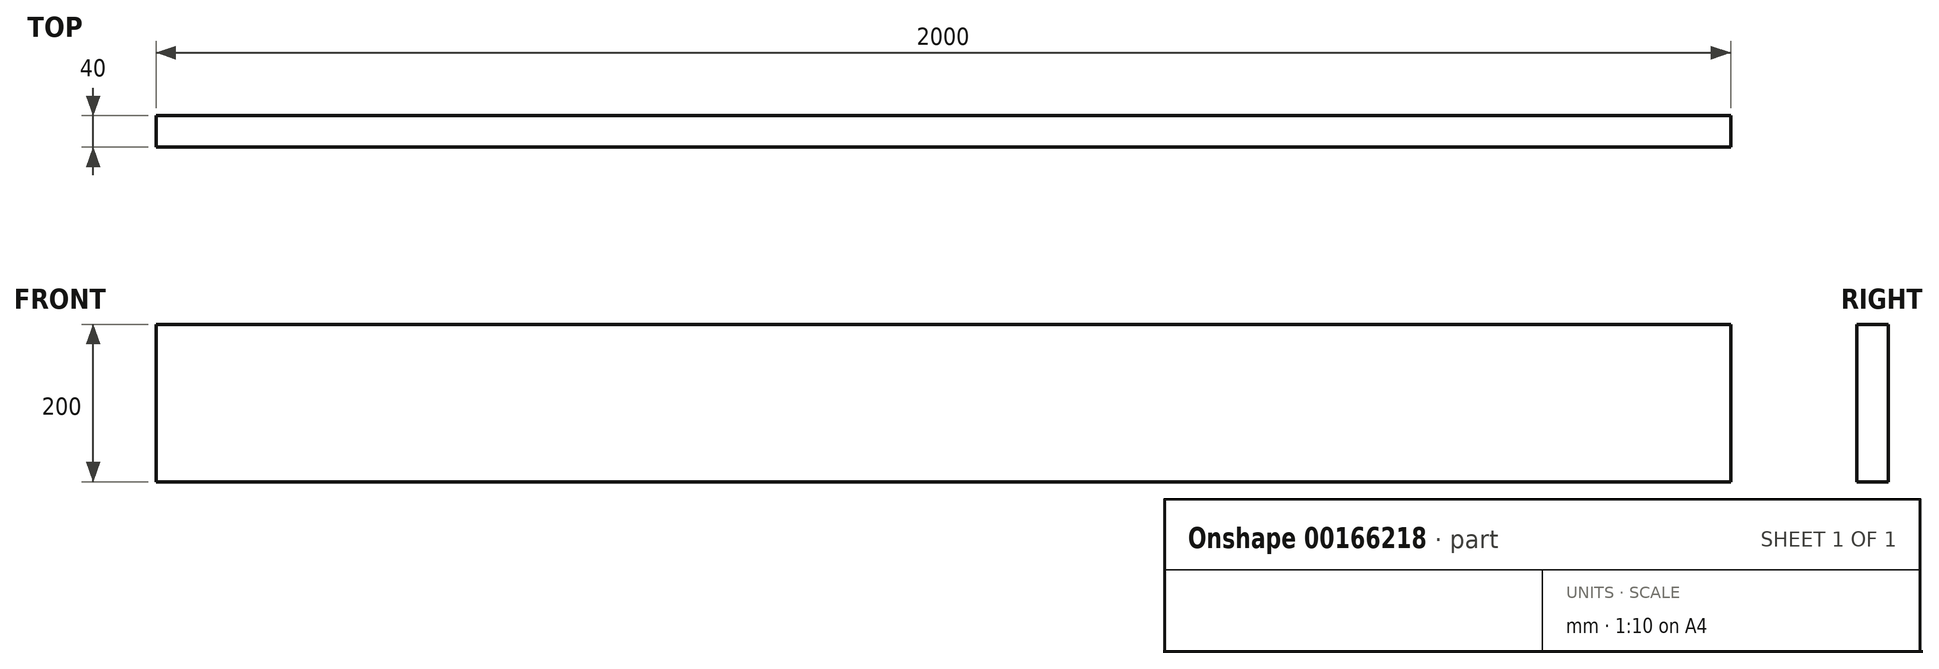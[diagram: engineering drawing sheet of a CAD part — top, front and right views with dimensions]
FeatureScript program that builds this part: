
annotation { "Feature Type Name" : "Feature", "Feature Type Description" : "" }
export const myFeature = defineFeature(function(context is Context, id is Id, definition is map)
    precondition{}
    {
        {
            var Q0;
            Q0=qCreatedBy(makeId("Front.planeOp"),FACE);
            var sketch = newSketch(context, id + "F0", { "sketchPlane" : qUnion([Q0])});
            skLineSegment(sketch, "E0.bottom", {"start": v(-1000, -100) * mm, "end": v(1000, -100) * mm});
            skLineSegment(sketch, "E0.top", {"start": v(-1000, 100) * mm, "end": v(1000, 100) * mm});
            skLineSegment(sketch, "E0.left", {"start": v(-1000, -100) * mm, "end": v(-1000, 100) * mm});
            skLineSegment(sketch, "E0.right", {"start": v(1000, -100) * mm, "end": v(1000, 100) * mm});
            skPoint(sketch, "E0.middle", {"position": v(0, 0) * mm});
            skSolve(sketch);
        }
        {
            var Q0;
            Q0=makeQuery(id+"F0.imprint","IMPRINT",FACE,{"disambiguationData":[TD([[makeQuery(id+"F0.imprint","IMPRINT",EDGE,{"derivedFrom":sQuery(id+"F0.wireOp",EDGE,"E0.bottom")}),1.0]])]});
            extrude(context, id + "F1", {"entities" : qUnion([Q0]), "depth" : 40 * mm, "symmetric" : true});
        }
    });
